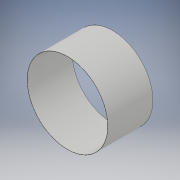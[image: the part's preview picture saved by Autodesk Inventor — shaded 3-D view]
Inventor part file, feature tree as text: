
AUTODESK INVENTOR PART (.ipt)
format: ipt  version: 2019 (Build 230136000, 136)  size: 103,936 bytes
history: native  units: mm
features: extrude x2, sketch x2
ambient origin geometry x8: Origin, YZ Plane, XZ Plane, XY Plane, X Axis, Y Axis, Z Axis, Center Point
bodies: Solid1 (feature_tree)
feature tree (4):
  extrude  "Extrusion1"  Depth=113.5mm TaperAngle=0.0deg
  extrude  "Extrusion2"  Depth=11.35mm TaperAngle=0.0deg
  sketch  "Sketch1"  dims[d0=203.7mm d1=113.5mm d2=0.0mm]
  sketch  "Sketch2"  dims[d3=202.7mm d4=11.35mm d5=0.0mm]
